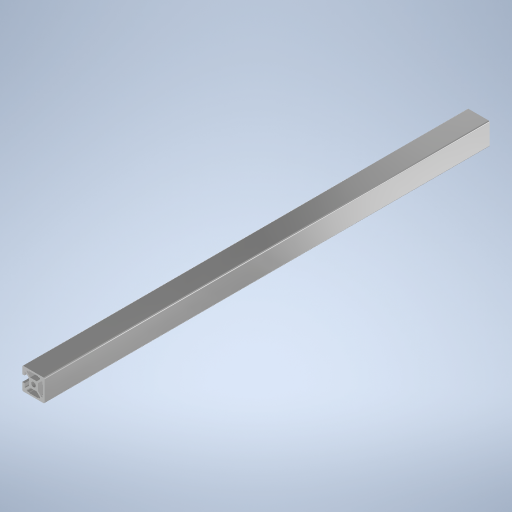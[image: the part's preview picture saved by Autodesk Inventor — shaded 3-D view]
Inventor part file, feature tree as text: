
AUTODESK INVENTOR PART (.ipt)
format: ipt  version: 2024 (Build 280153000, 153)  size: 371,712 bytes
history: native  units: mm
features: other x7, thread x2, sketch x2, extrude x1, hole x1
ambient origin geometry x8: Origin, YZ Plane, XZ Plane, XY Plane, X Axis, Y Axis, Z Axis, Center Point
bodies: Solid1 (feature_tree)
feature tree (13):
  extrude  "Extrusion1"  TaperAngle=0.0deg  [1 undecoded]
  hole  "Hole1"  [1 undecoded]
  other  "C1_XY"
  other  "C1_YZ"
  other  "C1_ZX"
  other  "C1_X"
  other  "C1_Y"
  other  "C1_Z"
  other  "C1_Center"
  thread  "Thread1"  [1 undecoded]
  thread  "Thread2"  [1 undecoded]
  sketch  "Sketch_66"  dims[d2=4.2mm d3=6.0mm d4=4.0mm d5=2.0mm d6=90.0deg d7=390.0mm d8=0.0mm d9=0.0mm d10=10.0mm d11=0.0mm d12=10.0mm d13=0.0mm]
  sketch  "Sketch2"  dims[d0=400.0mm d1=0.0mm]
note: 4 required parameter values undecoded (feature->parameter linkage not recoverable at this tier; creation-order binding heuristic only, values carry confidence <= 0.55)
